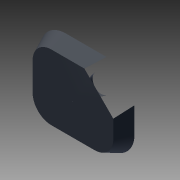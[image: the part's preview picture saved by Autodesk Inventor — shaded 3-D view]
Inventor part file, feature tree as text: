
AUTODESK INVENTOR PART (.ipt)
format: ipt  version: 2015 (Build 190159000, 159)  size: 275,968 bytes
history: native  units: in
note: dims shown in document units (in); Inventor stores cm internally (conversion verified against a paired STEP export)
features: other x2, extrude x1, imported_body x1
ambient origin geometry x8: Origin, YZ Plane, XZ Plane, XY Plane, X Axis, Y Axis, Z Axis, Center Point
bodies: Body1 (feature_tree)
feature tree (4):
  other  "Boss-Extrude3"
  other  "kinect base1"
  extrude  "Extrusion1"  Depth=0.001in TaperAngle=0.0deg
  imported_body  "Base1"
